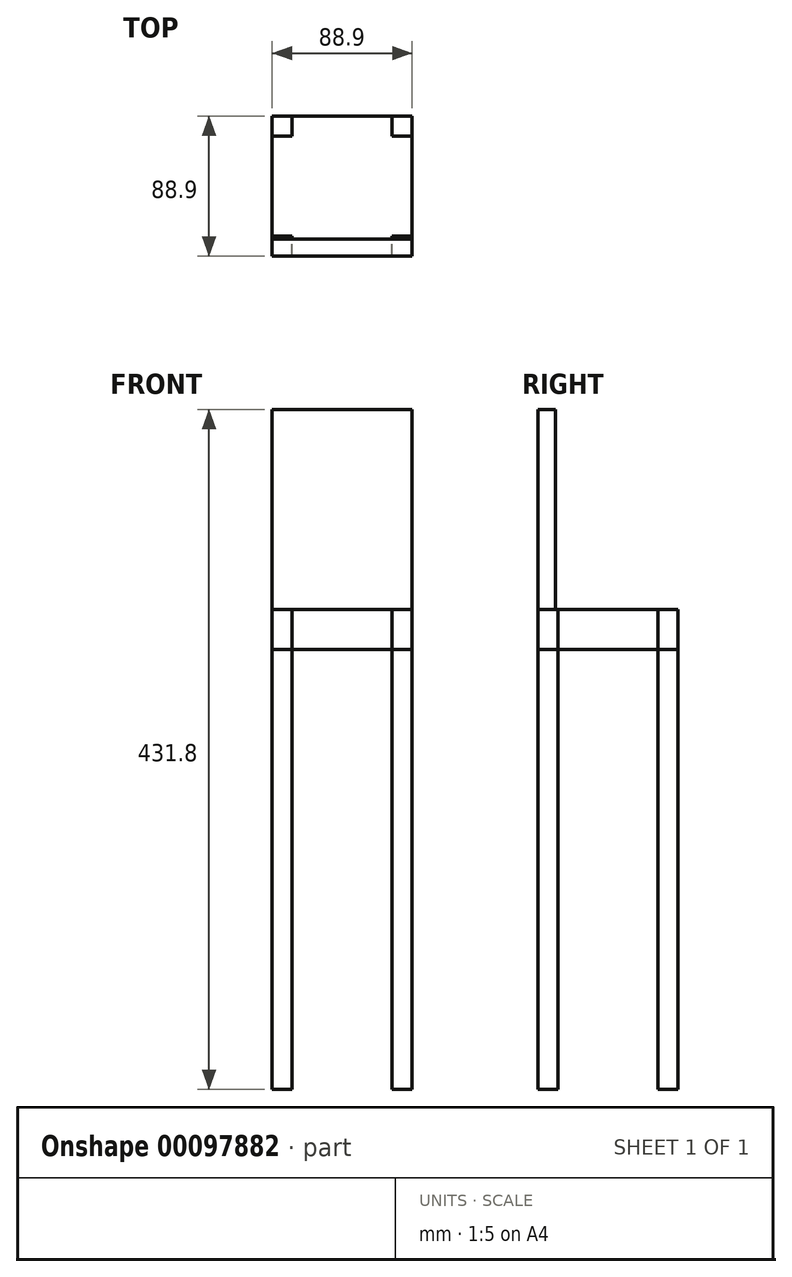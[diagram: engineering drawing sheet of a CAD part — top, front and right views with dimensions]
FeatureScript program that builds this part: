
annotation { "Feature Type Name" : "Feature", "Feature Type Description" : "" }
export const myFeature = defineFeature(function(context is Context, id is Id, definition is map)
    precondition{}
    {
        {
            var Q0;
            Q0=qCreatedBy(makeId("Top.planeOp"),FACE);
            var sketch = newSketch(context, id + "F0", { "sketchPlane" : qUnion([Q0])});
            skLineSegment(sketch, "E0.bottom", {"start": v(-31.75, 31.75) * mm, "end": v(-44.45, 31.75) * mm});
            skLineSegment(sketch, "E0.top", {"start": v(-31.75, 44.45) * mm, "end": v(-44.45, 44.45) * mm});
            skLineSegment(sketch, "E0.left", {"start": v(-31.75, 31.75) * mm, "end": v(-31.75, 44.45) * mm});
            skLineSegment(sketch, "E0.right", {"start": v(-44.45, 31.75) * mm, "end": v(-44.45, 44.45) * mm});
            skPoint(sketch, "E0.middle", {"position": v(-38.1, 38.1) * mm});
            skLineSegment(sketch, "E1.0.1.0", {"start": v(-44.45, -44.45) * mm, "end": v(-44.45, -31.75) * mm});
            skPoint(sketch, "E1.0.1.1", {"position": v(-38.1, -38.1) * mm});
            skLineSegment(sketch, "E1.0.1.2", {"start": v(-31.75, -44.45) * mm, "end": v(-31.75, -31.75) * mm});
            skLineSegment(sketch, "E1.0.1.3", {"start": v(-31.75, -31.75) * mm, "end": v(-44.45, -31.75) * mm});
            skLineSegment(sketch, "E1.0.1.4", {"start": v(-31.75, -44.45) * mm, "end": v(-44.45, -44.45) * mm});
            skLineSegment(sketch, "E1.1.0.0", {"start": v(31.75, 31.75) * mm, "end": v(31.75, 44.45) * mm});
            skPoint(sketch, "E1.1.0.1", {"position": v(38.1, 38.1) * mm});
            skLineSegment(sketch, "E1.1.0.2", {"start": v(44.45, 31.75) * mm, "end": v(44.45, 44.45) * mm});
            skLineSegment(sketch, "E1.1.0.3", {"start": v(44.45, 44.45) * mm, "end": v(31.75, 44.45) * mm});
            skLineSegment(sketch, "E1.1.0.4", {"start": v(44.45, 31.75) * mm, "end": v(31.75, 31.75) * mm});
            skLineSegment(sketch, "E1.1.1.0", {"start": v(31.75, -44.45) * mm, "end": v(31.75, -31.75) * mm});
            skPoint(sketch, "E1.1.1.1", {"position": v(38.1, -38.1) * mm});
            skLineSegment(sketch, "E1.1.1.2", {"start": v(44.45, -44.45) * mm, "end": v(44.45, -31.75) * mm});
            skLineSegment(sketch, "E1.1.1.3", {"start": v(44.45, -31.75) * mm, "end": v(31.75, -31.75) * mm});
            skLineSegment(sketch, "E1.1.1.4", {"start": v(44.45, -44.45) * mm, "end": v(31.75, -44.45) * mm});
            skLineSegment(sketch, "E1.direction1", {"start": v(-44.45, 31.75) * mm, "end": v(31.75, 31.75) * mm, "construction": true});
            skLineSegment(sketch, "E1.direction2", {"start": v(-44.45, 31.75) * mm, "end": v(-44.45, -44.45) * mm, "construction": true});
            skSolve(sketch);
        }
        {
            var Q0;
            Q0=makeQuery(id+"F0.imprint","IMPRINT",FACE,{"disambiguationData":[TD([[makeQuery(id+"F0.imprint","IMPRINT",EDGE,{"derivedFrom":sQuery(id+"F0.wireOp",EDGE,"E1.0.1.0")}),-1.0]])]});
            var Q1;
            Q1=makeQuery(id+"F0.imprint","IMPRINT",FACE,{"disambiguationData":[TD([[makeQuery(id+"F0.imprint","IMPRINT",EDGE,{"derivedFrom":sQuery(id+"F0.wireOp",EDGE,"E1.1.0.0")}),-1.0]])]});
            var Q2;
            Q2=makeQuery(id+"F0.imprint","IMPRINT",FACE,{"disambiguationData":[TD([[makeQuery(id+"F0.imprint","IMPRINT",EDGE,{"derivedFrom":sQuery(id+"F0.wireOp",EDGE,"E1.1.1.0")}),-1.0]])]});
            var Q3;
            Q3=makeQuery(id+"F0.imprint","IMPRINT",FACE,{"disambiguationData":[TD([[makeQuery(id+"F0.imprint","IMPRINT",EDGE,{"derivedFrom":sQuery(id+"F0.wireOp",EDGE,"E0.bottom")}),-1.0]])]});
            extrude(context, id + "F1", {"entities" : qUnion([Q0, Q1, Q2, Q3]), "depth" : 304.8 * mm});
        }
        {
            var Q0;
            Q0=makeQuery(id+"F1.opExtrude","CAP_FACE",FACE,{"disambiguationData":[OSD([sQuery(id+"F0.wireOp",EDGE,"E0.bottom"),sQuery(id+"F0.wireOp",EDGE,"E0.top"),sQuery(id+"F0.wireOp",EDGE,"E0.left"),sQuery(id+"F0.wireOp",EDGE,"E0.right")])],"isStart":false});
            var sketch = newSketch(context, id + "F2", { "sketchPlane" : qUnion([Q0])});
            skLineSegment(sketch, "E2.bottom", {"start": v(-44.45, 44.45) * mm, "end": v(44.45, 44.45) * mm});
            skLineSegment(sketch, "E2.top", {"start": v(-44.45, -44.45) * mm, "end": v(44.45, -44.45) * mm});
            skLineSegment(sketch, "E2.left", {"start": v(-44.45, 44.45) * mm, "end": v(-44.45, -44.45) * mm});
            skLineSegment(sketch, "E2.right", {"start": v(44.45, 44.45) * mm, "end": v(44.45, -44.45) * mm});
            skSolve(sketch);
        }
        {
            var Q0;
            {var subQ3=sQuery(id+"F2.wireOp",EDGE,"E2.top");Q0=makeQuery(id+"F2.imprint","IMPRINT",FACE,{"disambiguationData":[TD([[makeQuery(id+"F2.imprint","IMPRINT",EDGE,{"derivedFrom":subQ3}),1.0]])]});}
            var Q1;
            {var subQ4=makeQuery(id+"F1.opExtrude","CAP_EDGE",EDGE,{"disambiguationData":[OSD([sQuery(id+"F0.wireOp",EDGE,"E0.bottom")])],"isStart":false});Q1=makeQuery(id+"F2.imprint","IMPRINT",FACE,{"disambiguationData":[TD([[makeQuery(id+"F2.imprint","IMPRINT",EDGE,{"derivedFrom":subQ4}),-1.0]])]});}
            extrude(context, id + "F3", {"entities" : qUnion([Q0, Q1]), "oppositeDirection" : true, "depth" : 25.4 * mm});
        }
        {
            var Q0;
            Q0=makeQuery(id+"F3.opExtrude","CAP_FACE",FACE,{"disambiguationData":[OSD([sQuery(id+"F2.wireOp",EDGE,"E2.bottom"),sQuery(id+"F2.wireOp",EDGE,"E2.top"),sQuery(id+"F2.wireOp",EDGE,"E2.left"),sQuery(id+"F2.wireOp",EDGE,"E2.right")])],"isStart":true});
            var sketch = newSketch(context, id + "F4", { "sketchPlane" : qUnion([Q0])});
            skLineSegment(sketch, "E3.bottom", {"start": v(-44.45, -44.45) * mm, "end": v(44.45, -44.45) * mm});
            skLineSegment(sketch, "E3.top", {"start": v(-44.45, -33.5) * mm, "end": v(44.45, -33.5) * mm});
            skLineSegment(sketch, "E3.left", {"start": v(-44.45, -44.45) * mm, "end": v(-44.45, -33.5) * mm});
            skLineSegment(sketch, "E3.right", {"start": v(44.45, -44.45) * mm, "end": v(44.45, -33.5) * mm});
            skSolve(sketch);
        }
        {
            var Q0;
            Q0=makeQuery(id+"F4.imprint","IMPRINT",FACE,{"disambiguationData":[TD([[makeQuery(id+"F4.imprint","IMPRINT",EDGE,{"derivedFrom":sQuery(id+"F4.wireOp",EDGE,"E3.bottom")}),1.0]])]});
            extrude(context, id + "F5", {"entities" : qUnion([Q0]), "depth" : 127 * mm});
        }
    });
